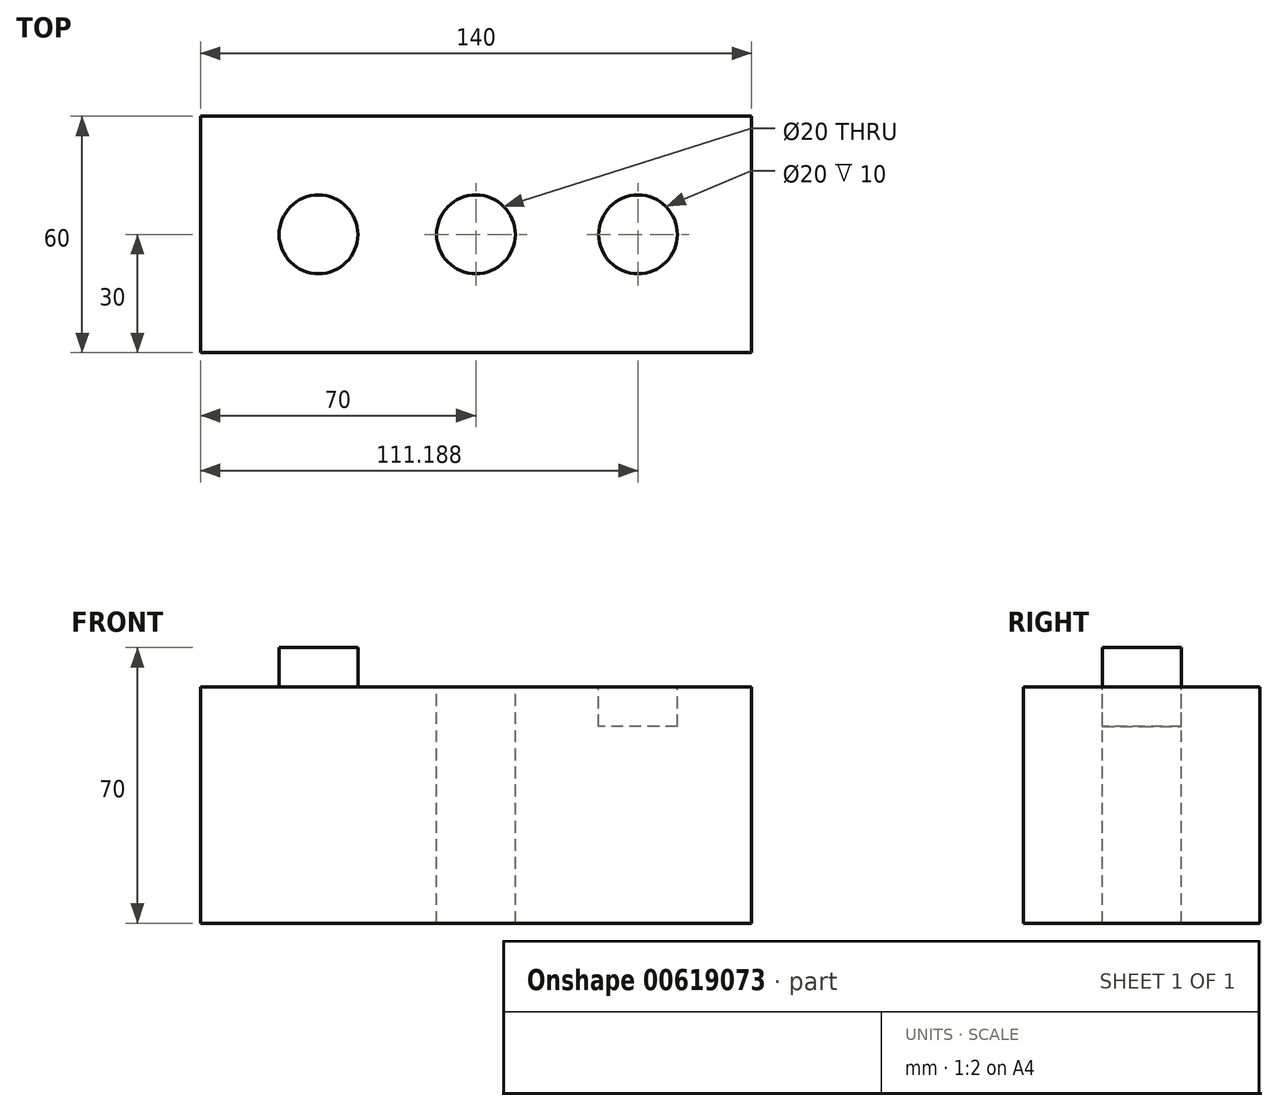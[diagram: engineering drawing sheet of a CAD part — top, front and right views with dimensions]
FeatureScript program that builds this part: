
annotation { "Feature Type Name" : "Feature", "Feature Type Description" : "" }
export const myFeature = defineFeature(function(context is Context, id is Id, definition is map)
    precondition{}
    {
        {
            var Q0;
            Q0=qCreatedBy(makeId("Front.planeOp"),FACE);
            var sketch = newSketch(context, id + "F0", { "sketchPlane" : qUnion([Q0])});
            skLineSegment(sketch, "E0.bottom", {"start": v(70, 30) * mm, "end": v(-70, 30) * mm});
            skLineSegment(sketch, "E0.top", {"start": v(70, -30) * mm, "end": v(-70, -30) * mm});
            skLineSegment(sketch, "E0.left", {"start": v(70, 30) * mm, "end": v(70, -30) * mm});
            skLineSegment(sketch, "E0.right", {"start": v(-70, 30) * mm, "end": v(-70, -30) * mm});
            skPoint(sketch, "E0.middle", {"position": v(0, 0) * mm});
            skSolve(sketch);
        }
        {
            var Q0;
            Q0=makeQuery(id+"F0.imprint","IMPRINT",FACE,{"disambiguationData":[TD([[makeQuery(id+"F0.imprint","IMPRINT",EDGE,{"derivedFrom":sQuery(id+"F0.wireOp",EDGE,"E0.bottom")}),1.0]])]});
            extrude(context, id + "F1", {"entities" : qUnion([Q0]), "endBound" : BoundingType.SYMMETRIC, "depth" : 60 * mm, "offsetDistance" : 25 * mm});
        }
        {
            var Q0;
            Q0=makeQuery(id+"F1.opExtrude","SWEPT_FACE",FACE,{"disambiguationData":[OSD([sQuery(id+"F0.wireOp",EDGE,"E0.bottom")])]});
            var sketch = newSketch(context, id + "F2", { "sketchPlane" : qUnion([Q0])});
            skCircle(sketch, "E1", {"center": v(0, 0) * mm, "radius": 10 * mm});
            skSolve(sketch);
        }
        {
            var Q0;
            Q0=makeQuery(id+"F2.imprint","IMPRINT",FACE,{"disambiguationData":[TD([[makeQuery(id+"F2.imprint","IMPRINT",EDGE,{"derivedFrom":sQuery(id+"F2.wireOp",EDGE,"E1")}),1.0]])]});
            extrude(context, id + "F3", {"entities" : qUnion([Q0]), "operationType" : NewBodyOperationType.REMOVE, "oppositeDirection" : true, "depth" : 63.9 * mm, "offsetDistance" : 25 * mm});
        }
        {
            var Q0;
            Q0=makeQuery(id+"F1.opExtrude","SWEPT_FACE",FACE,{"disambiguationData":[OSD([sQuery(id+"F0.wireOp",EDGE,"E0.bottom")])]});
            var sketch = newSketch(context, id + "F4", { "sketchPlane" : qUnion([Q0])});
            skCircle(sketch, "E2", {"center": v(41.19, 0) * mm, "radius": 10 * mm});
            skSolve(sketch);
        }
        {
            var Q0;
            Q0 = qSketchRegion(id + "F4", true);
            extrude(context, id + "F5", {"entities" : qUnion([Q0]), "operationType" : NewBodyOperationType.REMOVE, "oppositeDirection" : true, "depth" : 10 * mm, "offsetDistance" : 25 * mm});
        }
        {
            var Q0;
            Q0=makeQuery(id+"F1.opExtrude","SWEPT_FACE",FACE,{"disambiguationData":[OSD([sQuery(id+"F0.wireOp",EDGE,"E0.bottom")])]});
            var sketch = newSketch(context, id + "F6", { "sketchPlane" : qUnion([Q0])});
            skCircle(sketch, "E3", {"center": v(-40, 0) * mm, "radius": 10 * mm});
            skSolve(sketch);
        }
        {
            var Q0;
            Q0 = qSketchRegion(id + "F6", true);
            extrude(context, id + "F7", {"entities" : qUnion([Q0]), "operationType" : NewBodyOperationType.ADD, "depth" : 10 * mm, "offsetDistance" : 25 * mm});
        }
    });
